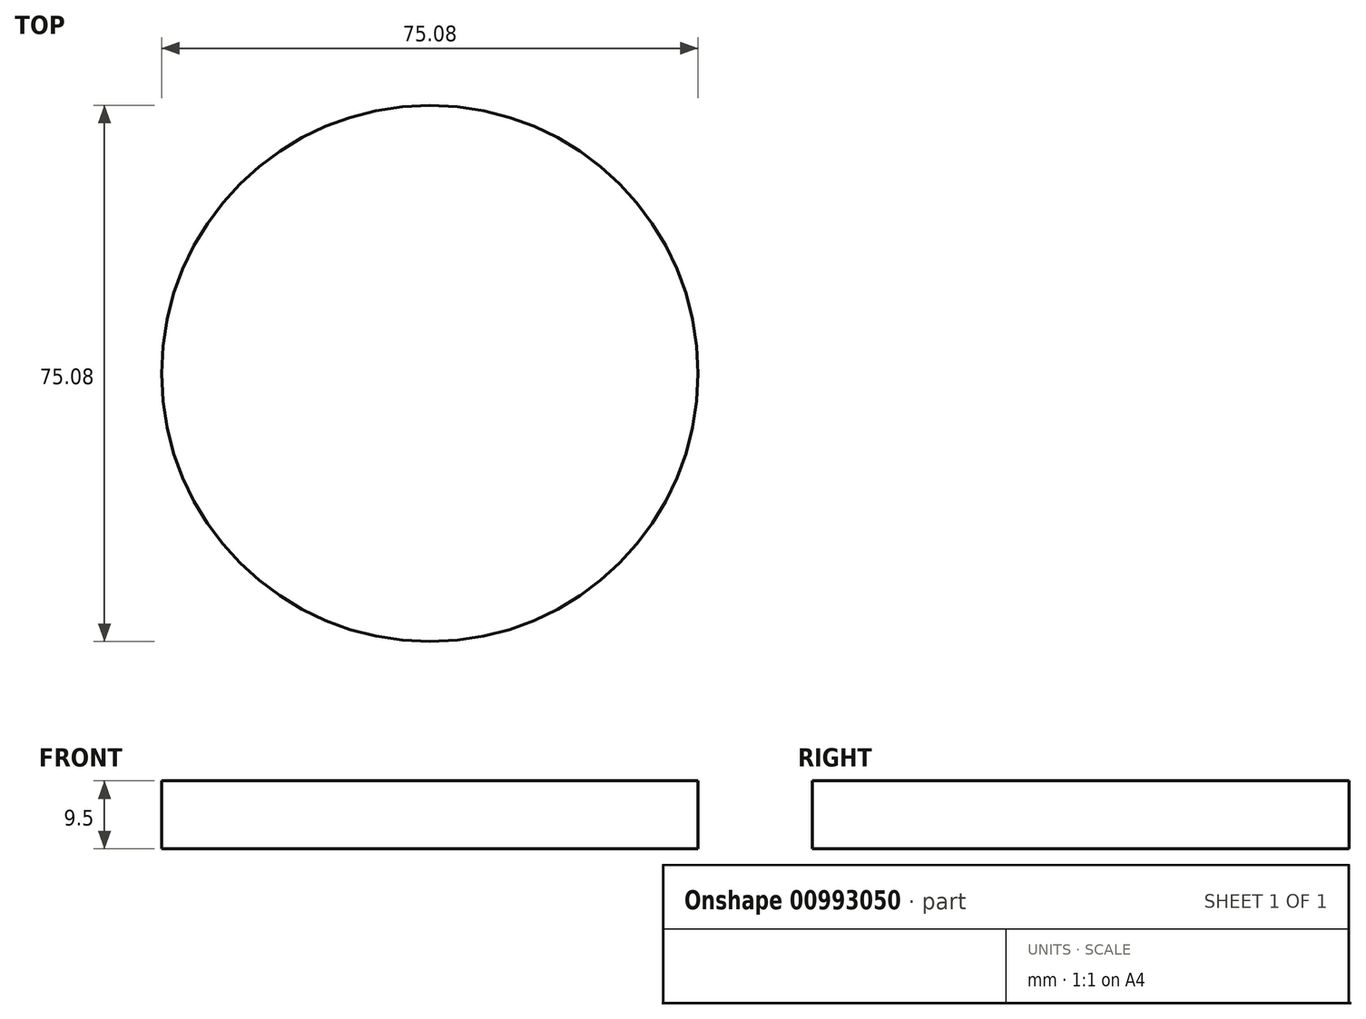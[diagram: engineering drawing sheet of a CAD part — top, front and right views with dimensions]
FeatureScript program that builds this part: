
annotation { "Feature Type Name" : "Feature", "Feature Type Description" : "" }
export const myFeature = defineFeature(function(context is Context, id is Id, definition is map)
    precondition{}
    {
        {
            var Q0;
            Q0=qCreatedBy(makeId("Top.planeOp"),FACE);
            var sketch = newSketch(context, id + "F0", { "sketchPlane" : qUnion([Q0])});
            skCircle(sketch, "E0", {"center": v(0, 0) * mm, "radius": 37.54 * mm});
            skSolve(sketch);
        }
        {
            var Q0;
            Q0=makeQuery(id+"F0.imprint","IMPRINT",FACE,{"disambiguationData":[TD([[makeQuery(id+"F0.imprint","IMPRINT",EDGE,{"derivedFrom":sQuery(id+"F0.wireOp",EDGE,"E0")}),1.0]])]});
            extrude(context, id + "F1", {"entities" : qUnion([Q0]), "depth" : 9.5 * mm, "offsetDistance" : 25.4 * mm});
        }
    });
